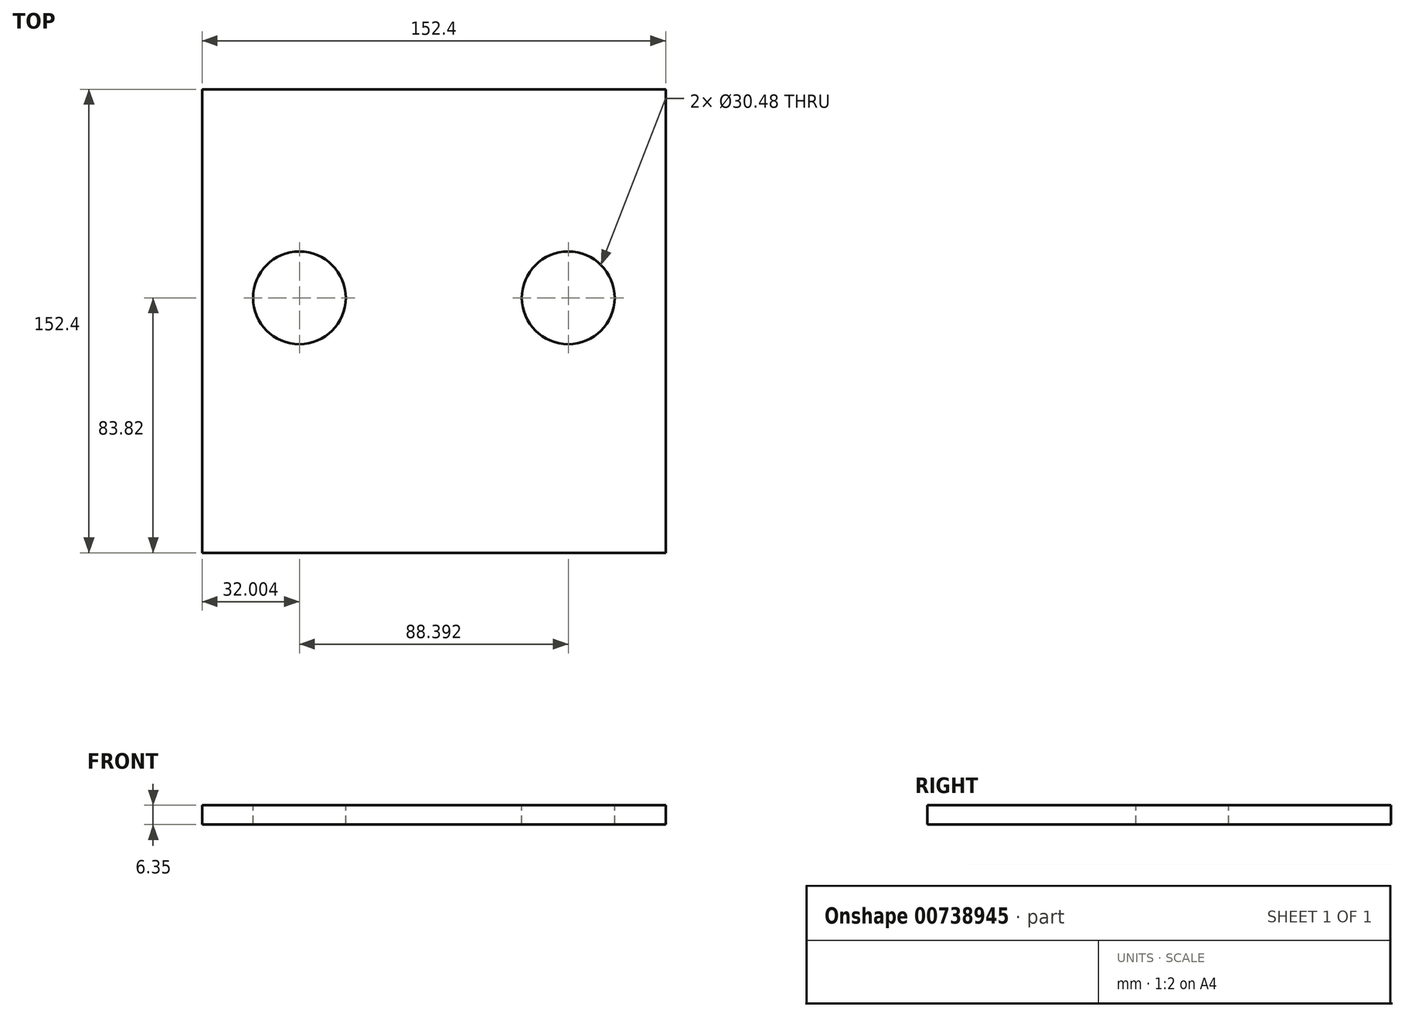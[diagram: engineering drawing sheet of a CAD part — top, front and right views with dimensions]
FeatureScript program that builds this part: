
annotation { "Feature Type Name" : "Feature", "Feature Type Description" : "" }
export const myFeature = defineFeature(function(context is Context, id is Id, definition is map)
    precondition{}
    {
        {
            var Q0;
            Q0=qCreatedBy(makeId("Top.planeOp"),FACE);
            var sketch = newSketch(context, id + "F0", { "sketchPlane" : qUnion([Q0])});
            skLineSegment(sketch, "E0.bottom", {"start": v(76.2, -76.2) * mm, "end": v(-76.2, -76.2) * mm});
            skLineSegment(sketch, "E0.top", {"start": v(76.2, 76.2) * mm, "end": v(-76.2, 76.2) * mm});
            skLineSegment(sketch, "E0.left", {"start": v(76.2, -76.2) * mm, "end": v(76.2, 76.2) * mm});
            skLineSegment(sketch, "E0.right", {"start": v(-76.2, -76.2) * mm, "end": v(-76.2, 76.2) * mm});
            skPoint(sketch, "E0.middle", {"position": v(0, 0) * mm});
            skPoint(sketch, "E1", {"position": v(-44.2, 7.62) * mm});
            skPoint(sketch, "E2", {"position": v(44.2, 7.62) * mm});
            skLineSegment(sketch, "E3", {"start": v(-44.2, 7.62) * mm, "end": v(-76.2, 7.62) * mm});
            skLineSegment(sketch, "E4", {"start": v(-44.2, 7.62) * mm, "end": v(-44.2, -76.2) * mm});
            skLineSegment(sketch, "E5", {"start": v(44.2, 7.62) * mm, "end": v(76.2, 7.62) * mm});
            skLineSegment(sketch, "E6", {"start": v(44.2, 7.62) * mm, "end": v(44.2, -76.2) * mm});
            skSolve(sketch);
        }
        {
            var Q0;
            {var subQ1=sQuery(id+"F0.wireOp",EDGE,"E0.top");Q0=makeQuery(id+"F0.imprint","IMPRINT",FACE,{"disambiguationData":[TD([[makeQuery(id+"F0.imprint","IMPRINT",EDGE,{"derivedFrom":subQ1}),1.0]])]});}
            var Q1;
            {var subQ4=sQuery(id+"F0.wireOp",EDGE,"E3");Q1=makeQuery(id+"F0.imprint","IMPRINT",FACE,{"disambiguationData":[TD([[makeQuery(id+"F0.imprint","IMPRINT",EDGE,{"derivedFrom":subQ4}),1.0]])]});}
            var Q2;
            {var subQ4=sQuery(id+"F0.wireOp",EDGE,"E5");Q2=makeQuery(id+"F0.imprint","IMPRINT",FACE,{"disambiguationData":[TD([[makeQuery(id+"F0.imprint","IMPRINT",EDGE,{"derivedFrom":subQ4}),-1.0]])]});}
            extrude(context, id + "F1", {"entities" : qUnion([Q0, Q1, Q2]), "depth" : 6.35 * mm, "offsetDistance" : 25.4 * mm});
        }
        {
            var Q0;
            Q0=makeQuery(id+"F1.opExtrude","CAP_FACE",FACE,{"disambiguationData":[OSD([sQuery(id+"F0.wireOp",EDGE,"E0.bottom"),sQuery(id+"F0.wireOp",EDGE,"E0.top"),sQuery(id+"F0.wireOp",EDGE,"E0.left"),sQuery(id+"F0.wireOp",EDGE,"E0.right")])],"isStart":false});
            var sketch = newSketch(context, id + "F2", { "sketchPlane" : qUnion([Q0])});
            skPoint(sketch, "E7", {"position": v(-44.2, 7.62) * mm});
            skPoint(sketch, "E8", {"position": v(44.2, 7.62) * mm});
            skLineSegment(sketch, "E9", {"start": v(-44.2, 7.62) * mm, "end": v(-44.2, -76.2) * mm});
            skLineSegment(sketch, "E10", {"start": v(-44.2, 7.62) * mm, "end": v(-76.2, 7.62) * mm});
            skLineSegment(sketch, "E11", {"start": v(44.2, 7.62) * mm, "end": v(76.2, 7.62) * mm});
            skLineSegment(sketch, "E12", {"start": v(44.2, 7.62) * mm, "end": v(44.2, -76.2) * mm});
            skSolve(sketch);
        }
        {
            var Q0;
            Q0=sQuery(id+"F2.wireOp",VERTEX,"E7");
            var Q1;
            Q1=sQuery(id+"F2.wireOp",VERTEX,"E8");
            var Q2;
            Q2=makeQuery(id+"F1.opExtrude","SWEPT_BODY",BODY,{"disambiguationData":[OSD([sQuery(id+"F0.wireOp",EDGE,"E0.bottom"),sQuery(id+"F0.wireOp",EDGE,"E0.top"),sQuery(id+"F0.wireOp",EDGE,"E0.left"),sQuery(id+"F0.wireOp",EDGE,"E0.right")])]});
            hole(context, id + "F3", {"style" : HoleStyle.SIMPLE, "endStyle" : HoleEndStyle.THROUGH, "holeDiameter" : 30.48 * mm, "majorDiameter" : 6.35 * mm, "isTappedThrough" : true, "tappedDepth" : 12.7 * mm, "tapClearance" : 3, "locations" : qUnion([Q0, Q1]), "scope" : qUnion([Q2])});
        }
    });
